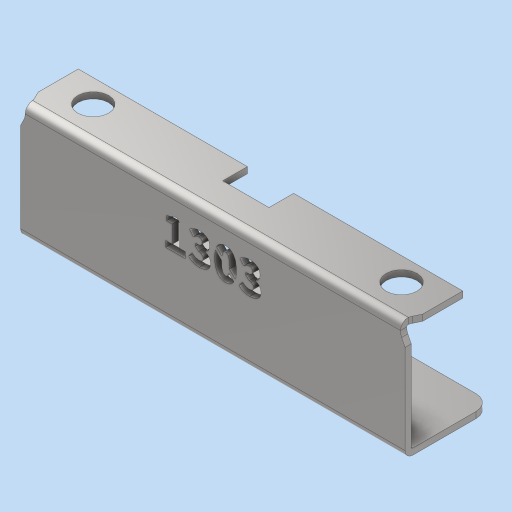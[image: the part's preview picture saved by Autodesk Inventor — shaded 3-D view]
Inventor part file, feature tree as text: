
AUTODESK INVENTOR PART (.ipt)
format: ipt  version: 2023 (Build 270158000, 158)  size: 581,120 bytes
history: native  units: mm
features: other x4, extrude x3, fillet x1, sketch x1, projected_geometry x1
ambient origin geometry x8: Origin, YZ Plane, XZ Plane, XY Plane, X Axis, Y Axis, Z Axis, Center Point
bodies: Body1 (feature_tree)
feature tree (10):
  other  "實體1"
  extrude  "擠出1"  Depth=124.7mm
  extrude  "擠出3"  Depth=26.3mm
  extrude  "擠出4"  Depth=33.0mm
  other  "折彎零件1"
  other  "折彎零件2"
  fillet  "圓角1"  Radius=17.0mm
  sketch  "草圖4"
  projected_geometry  "投影迴路1"
  other  "定義1"
